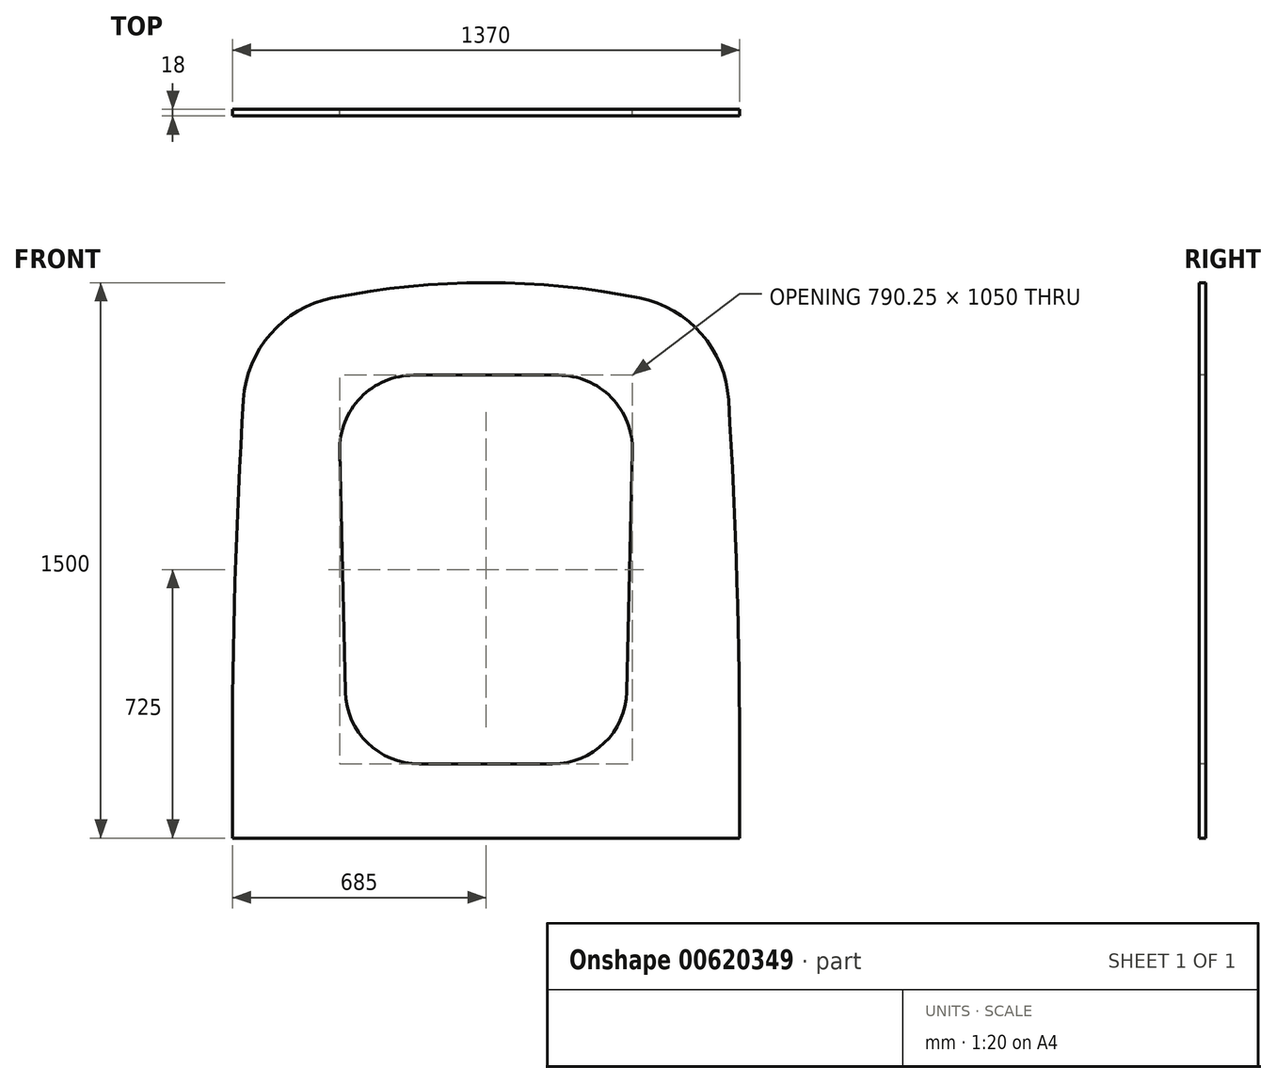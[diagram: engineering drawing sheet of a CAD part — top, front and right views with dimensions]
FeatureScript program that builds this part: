
annotation { "Feature Type Name" : "Feature", "Feature Type Description" : "" }
export const myFeature = defineFeature(function(context is Context, id is Id, definition is map)
    precondition{}
    {
        {
            var Q0;
            Q0=qCreatedBy(makeId("Front.planeOp"),FACE);
            var sketch = newSketch(context, id + "F0", { "sketchPlane" : qUnion([Q0])});
            skLineSegment(sketch, "E0", {"start": v(-685, 0) * mm, "end": v(685, 0) * mm});
            skLineSegment(sketch, "E1", {"start": v(-640, 1400) * mm, "end": v(640, 1400) * mm, "construction": true});
            skArc(sketch, "E2", {"start": v(640, 1400) * mm, "mid": v(0, 1500) * mm, "end": v(-640, 1400) * mm});
            skLineSegment(sketch, "E3", {"start": v(0, 1500) * mm, "end": v(0, 0) * mm, "construction": true});
            skPoint(sketch, "E3.endSnap0", {"position": v(0, 1500) * mm});
            skLineSegment(sketch, "E4", {"start": v(-685, 0) * mm, "end": v(-685, 200) * mm});
            skLineSegment(sketch, "E5", {"start": v(685, 0) * mm, "end": v(685, 200) * mm});
            skLineSegment(sketch, "E6", {"start": v(-685, 200) * mm, "end": v(685, 200) * mm, "construction": true});
            skArc(sketch, "E7", {"start": v(-640, 1400) * mm, "mid": v(-673.75, 800.42) * mm, "end": v(-685, 200) * mm});
            skArc(sketch, "E8", {"start": v(685, 200) * mm, "mid": v(673.75, 800.42) * mm, "end": v(640, 1400) * mm});
            skSolve(sketch);
        }
        {
            var Q0;
            Q0=makeQuery(id+"F0.imprint","IMPRINT",FACE,{"disambiguationData":[TD([[makeQuery(id+"F0.imprint","IMPRINT",EDGE,{"derivedFrom":sQuery(id+"F0.wireOp",EDGE,"E0")}),1.0]])]});
            extrude(context, id + "F1", {"entities" : qUnion([Q0]), "depth" : 18 * mm, "offsetDistance" : 25 * mm});
        }
        {
            var Q0;
            Q0=makeQuery(id+"F1.opExtrude","SWEPT_EDGE",EDGE,{"disambiguationData":[OSD([sQuery(id+"F0.wireOp",EDGE,"E2"),sQuery(id+"F0.wireOp",EDGE,"E7")])]});
            var Q1;
            Q1=makeQuery(id+"F1.opExtrude","SWEPT_EDGE",EDGE,{"disambiguationData":[OSD([sQuery(id+"F0.wireOp",EDGE,"E2"),sQuery(id+"F0.wireOp",EDGE,"E8")])]});
            fillet(context, id + "F2", {"entities" : qUnion([Q0, Q1]), "radius" : 300 * mm, "tangentPropagation" : true, "allowEdgeOverflow" : false});
        }
        {
            var Q0;
            Q0=makeQuery(id+"F1.opExtrude","CAP_FACE",FACE,{"disambiguationData":[OSD([sQuery(id+"F0.wireOp",EDGE,"E0"),sQuery(id+"F0.wireOp",EDGE,"E2"),sQuery(id+"F0.wireOp",EDGE,"E4"),sQuery(id+"F0.wireOp",EDGE,"E5"),sQuery(id+"F0.wireOp",EDGE,"E7"),sQuery(id+"F0.wireOp",EDGE,"E8")])],"isStart":false});
            var sketch = newSketch(context, id + "F3", { "sketchPlane" : qUnion([Q0])});
            skLineSegment(sketch, "E9", {"start": v(-400, 1250) * mm, "end": v(400, 1250) * mm});
            skLineSegment(sketch, "E10", {"start": v(400, 1250) * mm, "end": v(375, 200) * mm});
            skLineSegment(sketch, "E11", {"start": v(375, 200) * mm, "end": v(-375, 200) * mm});
            skLineSegment(sketch, "E12", {"start": v(-375, 200) * mm, "end": v(-400, 1250) * mm});
            skLineSegment(sketch, "E13", {"start": v(0, 1250) * mm, "end": v(0, 200) * mm, "construction": true});
            skSolve(sketch);
        }
        {
            var Q0;
            Q0=makeQuery(id+"F3.imprint","IMPRINT",FACE,{"disambiguationData":[TD([[makeQuery(id+"F3.imprint","IMPRINT",EDGE,{"derivedFrom":sQuery(id+"F3.wireOp",EDGE,"E9")}),-1.0]])]});
            extrude(context, id + "F4", {"entities" : qUnion([Q0]), "operationType" : NewBodyOperationType.REMOVE, "oppositeDirection" : true, "depth" : 25 * mm, "offsetDistance" : 25 * mm});
        }
        {
            var Q0;
            Q0=makeQuery(id+"F4.boolean.opBoolean","COPY",EDGE,{"derivedFrom":makeQuery(id+"F4.opExtrude","SWEPT_EDGE",EDGE,{"disambiguationData":[OSD([sQuery(id+"F3.wireOp",EDGE,"E9"),sQuery(id+"F3.wireOp",EDGE,"E10")])]})});
            var Q1;
            Q1=makeQuery(id+"F4.boolean.opBoolean","COPY",EDGE,{"derivedFrom":makeQuery(id+"F4.opExtrude","SWEPT_EDGE",EDGE,{"disambiguationData":[OSD([sQuery(id+"F3.wireOp",EDGE,"E9"),sQuery(id+"F3.wireOp",EDGE,"E12")])]})});
            var Q2;
            Q2=makeQuery(id+"F4.boolean.opBoolean","COPY",EDGE,{"derivedFrom":makeQuery(id+"F4.opExtrude","SWEPT_EDGE",EDGE,{"disambiguationData":[OSD([sQuery(id+"F3.wireOp",EDGE,"E11"),sQuery(id+"F3.wireOp",EDGE,"E12")])]})});
            var Q3;
            Q3=makeQuery(id+"F4.boolean.opBoolean","COPY",EDGE,{"derivedFrom":makeQuery(id+"F4.opExtrude","SWEPT_EDGE",EDGE,{"disambiguationData":[OSD([sQuery(id+"F3.wireOp",EDGE,"E10"),sQuery(id+"F3.wireOp",EDGE,"E11")])]})});
            fillet(context, id + "F5", {"entities" : qUnion([Q0, Q1, Q2, Q3]), "radius" : 200 * mm, "tangentPropagation" : true, "allowEdgeOverflow" : false});
        }
    });
